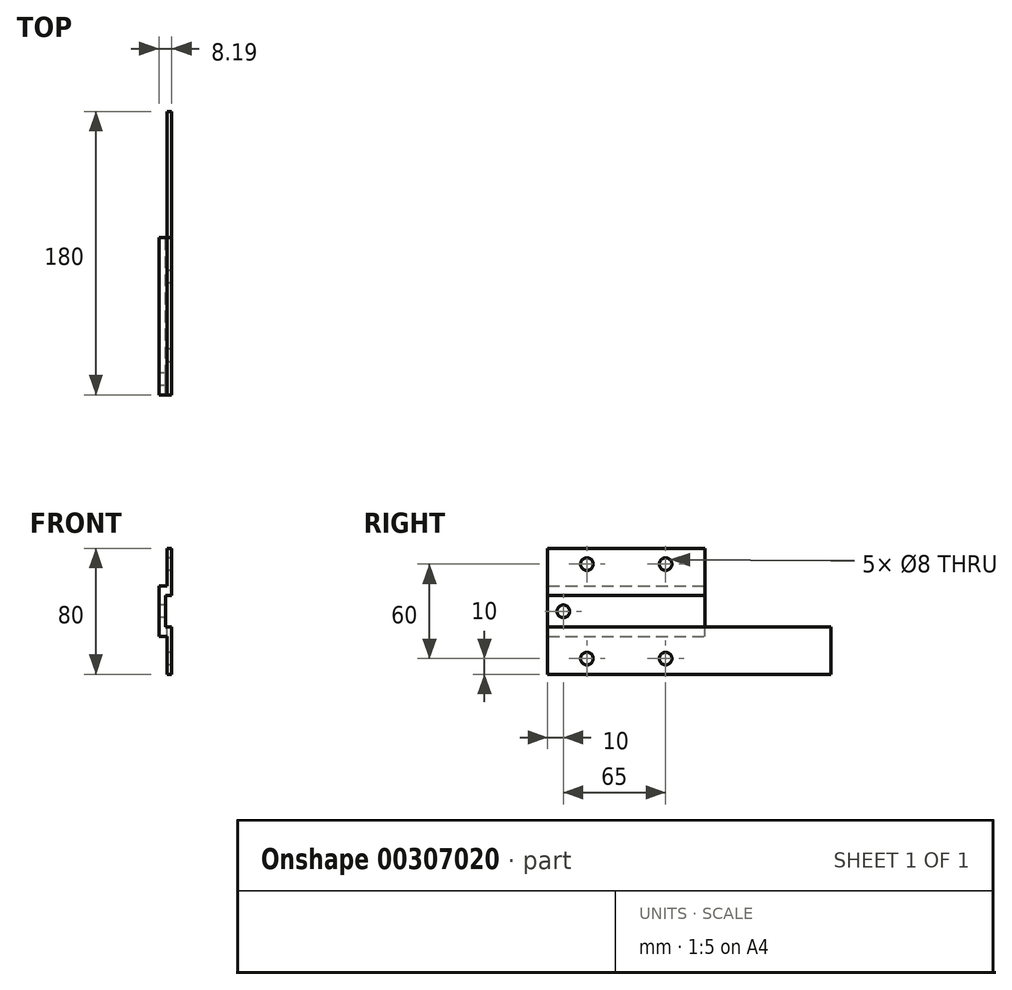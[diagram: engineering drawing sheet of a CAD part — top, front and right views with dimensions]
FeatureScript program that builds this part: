
annotation { "Feature Type Name" : "Feature", "Feature Type Description" : "" }
export const myFeature = defineFeature(function(context is Context, id is Id, definition is map)
    precondition{}
    {
        {
            var Q0;
            Q0=qCreatedBy(makeId("Front.planeOp"),FACE);
            var sketch = newSketch(context, id + "F0", { "sketchPlane" : qUnion([Q0])});
            skLineSegment(sketch, "E0", {"start": v(0, 40) * mm, "end": v(0, 16) * mm});
            skLineSegment(sketch, "E1", {"start": v(0, 16) * mm, "end": v(-5.19, 16) * mm});
            skLineSegment(sketch, "E2", {"start": v(-5.19, 16) * mm, "end": v(-5.19, 0) * mm});
            skLineSegment(sketch, "E3", {"start": v(-5.19, 0) * mm, "end": v(-1, 0) * mm});
            skLineSegment(sketch, "E4", {"start": v(-1, 0) * mm, "end": v(-1, 10) * mm});
            skLineSegment(sketch, "E5", {"start": v(-1, 10) * mm, "end": v(3, 10) * mm});
            skLineSegment(sketch, "E6", {"start": v(3, 10) * mm, "end": v(3, 40) * mm});
            skLineSegment(sketch, "E7", {"start": v(3, 40) * mm, "end": v(0, 40) * mm});
            skLineSegment(sketch, "E8.MirrorCS", {"start": v(0, -16) * mm, "end": v(-5.19, -16) * mm});
            skLineSegment(sketch, "E9.MirrorCS", {"start": v(-1, -10) * mm, "end": v(3, -10) * mm});
            skLineSegment(sketch, "E10.MirrorCS", {"start": v(0, -40) * mm, "end": v(0, -16) * mm});
            skLineSegment(sketch, "E11.MirrorCS", {"start": v(3, -10) * mm, "end": v(3, -40) * mm});
            skLineSegment(sketch, "E12.MirrorCS", {"start": v(3, -40) * mm, "end": v(0, -40) * mm});
            skLineSegment(sketch, "E13.MirrorCS", {"start": v(-5.19, -16) * mm, "end": v(-5.19, 0) * mm});
            skLineSegment(sketch, "E14.MirrorCS", {"start": v(-1, 0) * mm, "end": v(-1, -10) * mm});
            skSolve(sketch);
        }
        {
            var Q0;
            Q0 = qSketchRegion(id + "F0", true);
            extrude(context, id + "F1", {"entities" : qUnion([Q0]), "depth" : 180 * mm});
        }
        {
            var Q0;
            Q0=makeQuery(id+"F1.opExtrude","SWEPT_FACE",FACE,{"disambiguationData":[OSD([sQuery(id+"F0.wireOp",EDGE,"E2"),sQuery(id+"F0.wireOp",EDGE,"E13.MirrorCS")])]});
            var sketch = newSketch(context, id + "F2", { "sketchPlane" : qUnion([Q0])});
            skCircle(sketch, "E15", {"center": v(170, 0) * mm, "radius": 4 * mm});
            skCircle(sketch, "E16", {"center": v(155, 30) * mm, "radius": 4 * mm});
            skCircle(sketch, "E17", {"center": v(105, 30) * mm, "radius": 4 * mm});
            skCircle(sketch, "E18.MirrorC", {"center": v(155, -30) * mm, "radius": 4 * mm});
            skCircle(sketch, "E19.MirrorC", {"center": v(105, -30) * mm, "radius": 4 * mm});
            skSolve(sketch);
        }
        {
            var Q0;
            Q0 = qSketchRegion(id + "F2", true);
            extrude(context, id + "F3", {"entities" : qUnion([Q0]), "operationType" : NewBodyOperationType.REMOVE, "oppositeDirection" : true, "depth" : 25 * mm});
        }
        {
            var Q0;
            Q0=makeQuery(id+"F1.opExtrude","SWEPT_FACE",FACE,{"disambiguationData":[OSD([sQuery(id+"F0.wireOp",EDGE,"E4"),sQuery(id+"F0.wireOp",EDGE,"E14.MirrorCS")])]});
            var sketch = newSketch(context, id + "F4", { "sketchPlane" : qUnion([Q0])});
            skLineSegment(sketch, "E20", {"start": v(0, 40) * mm, "end": v(0, -10) * mm});
            skLineSegment(sketch, "E21", {"start": v(0, -10) * mm, "end": v(-80, -10) * mm});
            skLineSegment(sketch, "E22", {"start": v(-80, -10) * mm, "end": v(-80, 40) * mm});
            skLineSegment(sketch, "E23", {"start": v(-80, 40) * mm, "end": v(0, 40) * mm});
            skSolve(sketch);
        }
        {
            var Q0;
            Q0 = qSketchRegion(id + "F4", true);
            extrude(context, id + "F5", {"entities" : qUnion([Q0]), "operationType" : NewBodyOperationType.REMOVE, "oppositeDirection" : true, "depth" : 25 * mm, "symmetric" : true});
        }
        {
            var Q0;
            Q0=makeQuery(id+"F1.opExtrude","CAP_FACE",FACE,{"disambiguationData":[OSD([sQuery(id+"F0.wireOp",EDGE,"E0"),sQuery(id+"F0.wireOp",EDGE,"E1"),sQuery(id+"F0.wireOp",EDGE,"E2"),sQuery(id+"F0.wireOp",EDGE,"E4"),sQuery(id+"F0.wireOp",EDGE,"E5"),sQuery(id+"F0.wireOp",EDGE,"E6"),sQuery(id+"F0.wireOp",EDGE,"E7"),sQuery(id+"F0.wireOp",EDGE,"E8.MirrorCS"),sQuery(id+"F0.wireOp",EDGE,"E9.MirrorCS"),sQuery(id+"F0.wireOp",EDGE,"E10.MirrorCS"),sQuery(id+"F0.wireOp",EDGE,"E11.MirrorCS"),sQuery(id+"F0.wireOp",EDGE,"E12.MirrorCS"),sQuery(id+"F0.wireOp",EDGE,"E13.MirrorCS"),sQuery(id+"F0.wireOp",EDGE,"E14.MirrorCS")])],"isStart":true});
            var sketch = newSketch(context, id + "F6", { "sketchPlane" : qUnion([Q0])});
            skPoint(sketch, "E24.oppositeSnap0", {"position": v(1.1, -10) * mm});
            skLineSegment(sketch, "E24.bottom", {"start": v(5.19, -16) * mm, "end": v(0, -16) * mm});
            skLineSegment(sketch, "E24.top", {"start": v(5.19, -10) * mm, "end": v(0, -10) * mm});
            skLineSegment(sketch, "E24.left", {"start": v(5.19, -16) * mm, "end": v(5.19, -10) * mm});
            skLineSegment(sketch, "E24.right", {"start": v(0, -16) * mm, "end": v(0, -10) * mm});
            skSolve(sketch);
        }
        {
            var Q0;
            Q0 = qSketchRegion(id + "F6", true);
            extrude(context, id + "F7", {"entities" : qUnion([Q0]), "operationType" : NewBodyOperationType.REMOVE, "oppositeDirection" : true, "depth" : 80 * mm});
        }
    });
